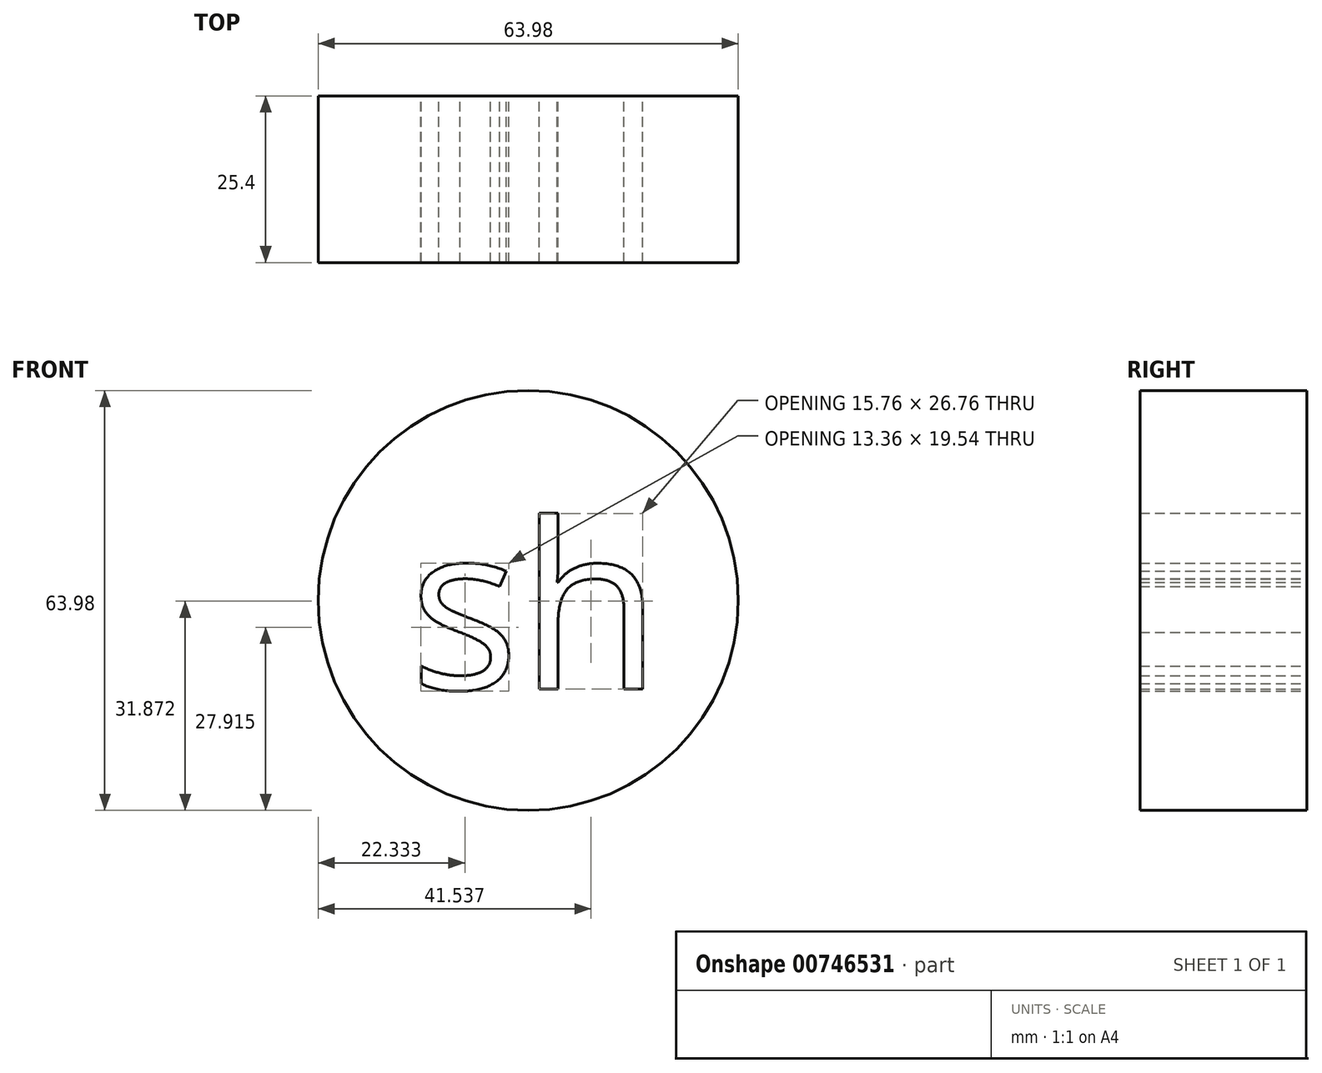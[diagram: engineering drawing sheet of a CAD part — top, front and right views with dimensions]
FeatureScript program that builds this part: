
annotation { "Feature Type Name" : "Feature", "Feature Type Description" : "" }
export const myFeature = defineFeature(function(context is Context, id is Id, definition is map)
    precondition{}
    {
        {
            var Q0;
            Q0=qCreatedBy(makeId("Front.planeOp"),FACE);
            var sketch = newSketch(context, id + "F0", { "sketchPlane" : qUnion([Q0])});
            skCircle(sketch, "E0", {"center": v(0, 0) * mm, "radius": 31.99 * mm});
            skText(sketch, "E1", { "text": "sh\n", "fontName": "OpenSans-Regular.ttf"});
            const initialGuessF0  = {"E1": [-0.01816, -0.0135, 1, 0, 0.02536]};
            skSetInitialGuess(sketch, initialGuessF0);
            skSolve(sketch);
        }
        {
            var Q0;
            Q0 = qSketchRegion(id + "F0", true);
            extrude(context, id + "F1", {"entities" : qUnion([Q0]), "depth" : 25.4 * mm, "offsetDistance" : 25.4 * mm});
        }
    });
